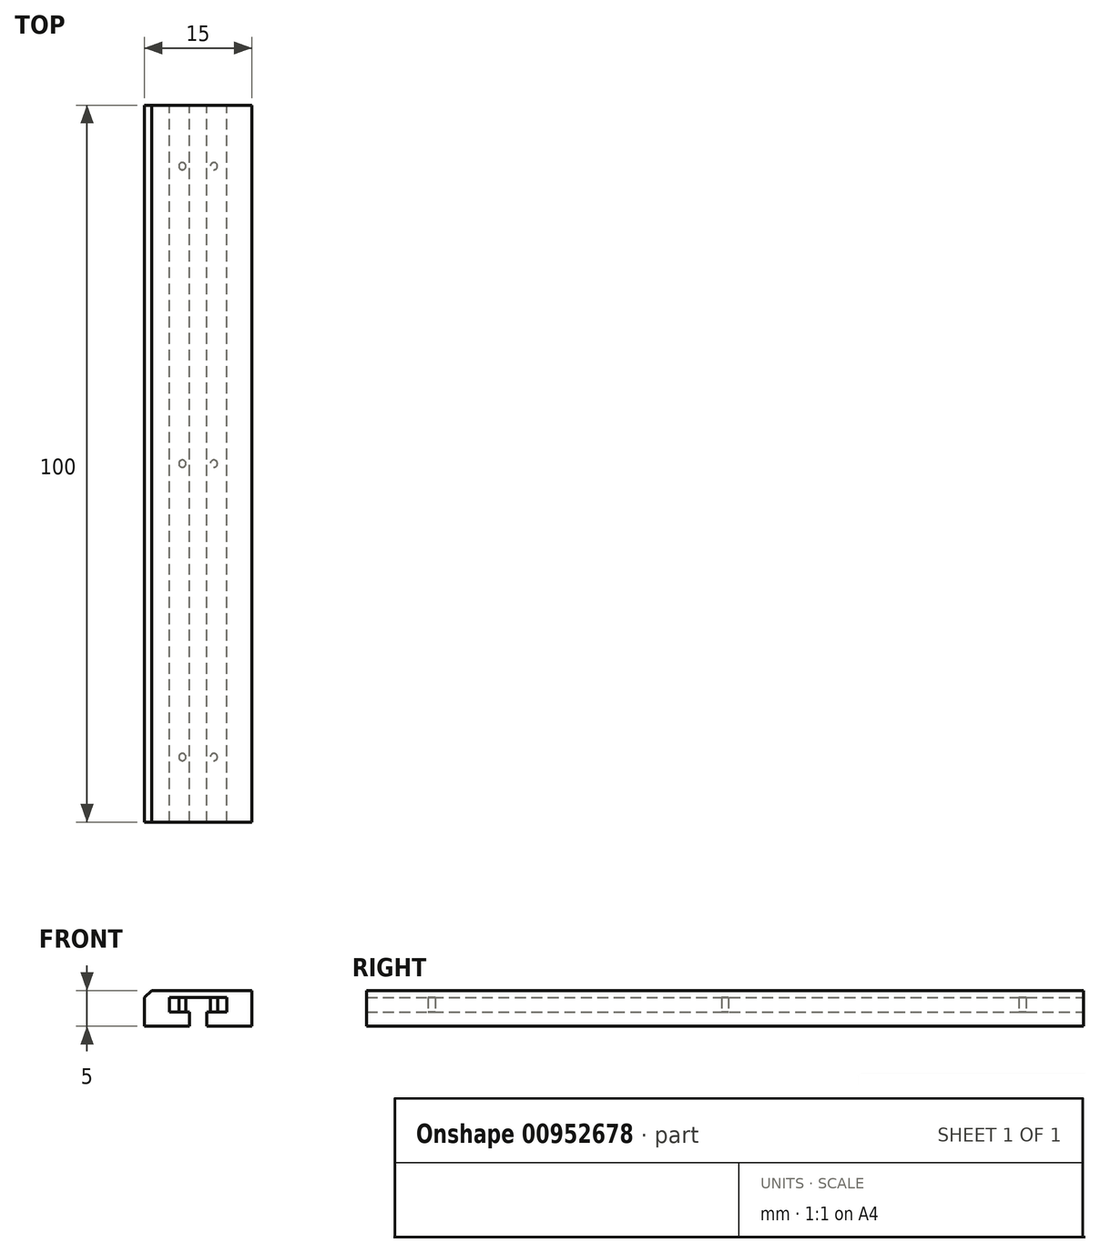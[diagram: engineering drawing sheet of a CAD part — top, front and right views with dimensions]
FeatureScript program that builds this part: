
annotation { "Feature Type Name" : "Feature", "Feature Type Description" : "" }
export const myFeature = defineFeature(function(context is Context, id is Id, definition is map)
    precondition{}
    {
        {
            var Q0;
            Q0=qCreatedBy(makeId("Front.planeOp"),FACE);
            var sketch = newSketch(context, id + "F0", { "sketchPlane" : qUnion([Q0])});
            skLineSegment(sketch, "E0.bottom", {"start": v(-7.5, 0) * mm, "end": v(7.5, 0) * mm});
            skLineSegment(sketch, "E0.top", {"start": v(-7.5, 5) * mm, "end": v(7.5, 5) * mm});
            skLineSegment(sketch, "E0.left", {"start": v(-7.5, 0) * mm, "end": v(-7.5, 5) * mm});
            skLineSegment(sketch, "E0.right", {"start": v(7.5, 0) * mm, "end": v(7.5, 5) * mm});
            skPoint(sketch, "E1", {"position": v(0, 0) * mm});
            skSolve(sketch);
        }
        {
            var Q0;
            Q0 = qSketchRegion(id + "F0", true);
            extrude(context, id + "F1", {"entities" : qUnion([Q0]), "depth" : 100 * mm, "offsetDistance" : 25 * mm});
        }
        {
            var Q0;
            Q0=makeQuery(id+"F1.opExtrude","CAP_FACE",FACE,{"disambiguationData":[OSD([sQuery(id+"F0.wireOp",EDGE,"E0.bottom"),sQuery(id+"F0.wireOp",EDGE,"E0.top"),sQuery(id+"F0.wireOp",EDGE,"E0.left"),sQuery(id+"F0.wireOp",EDGE,"E0.right")])],"isStart":true});
            var sketch = newSketch(context, id + "F2", { "sketchPlane" : qUnion([Q0])});
            skLineSegment(sketch, "E2.bottom", {"start": v(-1.2, 2) * mm, "end": v(0, 2) * mm});
            skLineSegment(sketch, "E2.top", {"start": v(-1.2, 0) * mm, "end": v(0, 0) * mm});
            skLineSegment(sketch, "E2.left", {"start": v(-1.2, 2) * mm, "end": v(-1.2, 0) * mm});
            skLineSegment(sketch, "E2.right", {"start": v(0, 2) * mm, "end": v(0, 0) * mm});
            skLineSegment(sketch, "E3.MirrorCS", {"start": v(1.2, 2) * mm, "end": v(1.2, 0) * mm});
            skLineSegment(sketch, "E4.MirrorCS", {"start": v(1.2, 2) * mm, "end": v(0, 2) * mm});
            skLineSegment(sketch, "E5.MirrorCS", {"start": v(1.2, 0) * mm, "end": v(0, 0) * mm});
            skLineSegment(sketch, "E6.bottom", {"start": v(0, 2) * mm, "end": v(-4, 2) * mm});
            skLineSegment(sketch, "E6.top", {"start": v(0, 4) * mm, "end": v(-4, 4) * mm});
            skLineSegment(sketch, "E6.left", {"start": v(0, 2) * mm, "end": v(0, 4) * mm});
            skLineSegment(sketch, "E6.right", {"start": v(-4, 2) * mm, "end": v(-4, 4) * mm});
            skLineSegment(sketch, "E7.MirrorCS", {"start": v(0, 4) * mm, "end": v(4, 4) * mm});
            skLineSegment(sketch, "E8.MirrorCS", {"start": v(4, 2) * mm, "end": v(4, 4) * mm});
            skLineSegment(sketch, "E9.MirrorCS", {"start": v(0, 2) * mm, "end": v(4, 2) * mm});
            skSolve(sketch);
        }
        {
            var Q0;
            Q0 = qSketchRegion(id + "F2", true);
            extrude(context, id + "F3", {"entities" : qUnion([Q0]), "operationType" : NewBodyOperationType.REMOVE, "oppositeDirection" : true, "depth" : 113.7 * mm, "offsetDistance" : 25 * mm});
        }
        {
            var Q0;
            Q0=makeQuery(id+"F3.boolean.opBoolean","COPY",FACE,{"derivedFrom":makeQuery(id+"F3.opExtrude","SWEPT_FACE",FACE,{"disambiguationData":[OSD([sQuery(id+"F2.wireOp",EDGE,"E9.MirrorCS")])]})});
            var sketch = newSketch(context, id + "F4", { "sketchPlane" : qUnion([Q0])});
            skCircle(sketch, "E10", {"center": v(-2.2, -8.5) * mm, "radius": 0.5 * mm});
            skCircle(sketch, "E11", {"center": v(-2.2, -50) * mm, "radius": 0.5 * mm});
            skPoint(sketch, "E11.centerSnap0", {"position": v(-4, -50) * mm});
            skCircle(sketch, "E12", {"center": v(-2.2, -90.95) * mm, "radius": 0.5 * mm});
            skCircle(sketch, "E13", {"center": v(2.2, -90.95) * mm, "radius": 0.5 * mm});
            skCircle(sketch, "E14", {"center": v(2.2, -50) * mm, "radius": 0.5 * mm});
            skCircle(sketch, "E15", {"center": v(2.2, -8.5) * mm, "radius": 0.5 * mm});
            skSolve(sketch);
        }
        {
            var Q0;
            Q0 = qSketchRegion(id + "F4", true);
            extrude(context, id + "F5", {"entities" : qUnion([Q0]), "operationType" : NewBodyOperationType.ADD, "depth" : 2.87 * mm, "offsetDistance" : 25 * mm});
        }
        {
            var Q0;
            Q0=makeQuery(id+"F1.opExtrude","SWEPT_EDGE",EDGE,{"disambiguationData":[OSD([sQuery(id+"F0.wireOp",EDGE,"E0.top"),sQuery(id+"F0.wireOp",EDGE,"E0.left")])]});
            chamfer(context, id + "F6", {"entities" : qUnion([Q0]), "width" : 1 * mm, "tangentPropagation" : true});
        }
    });
